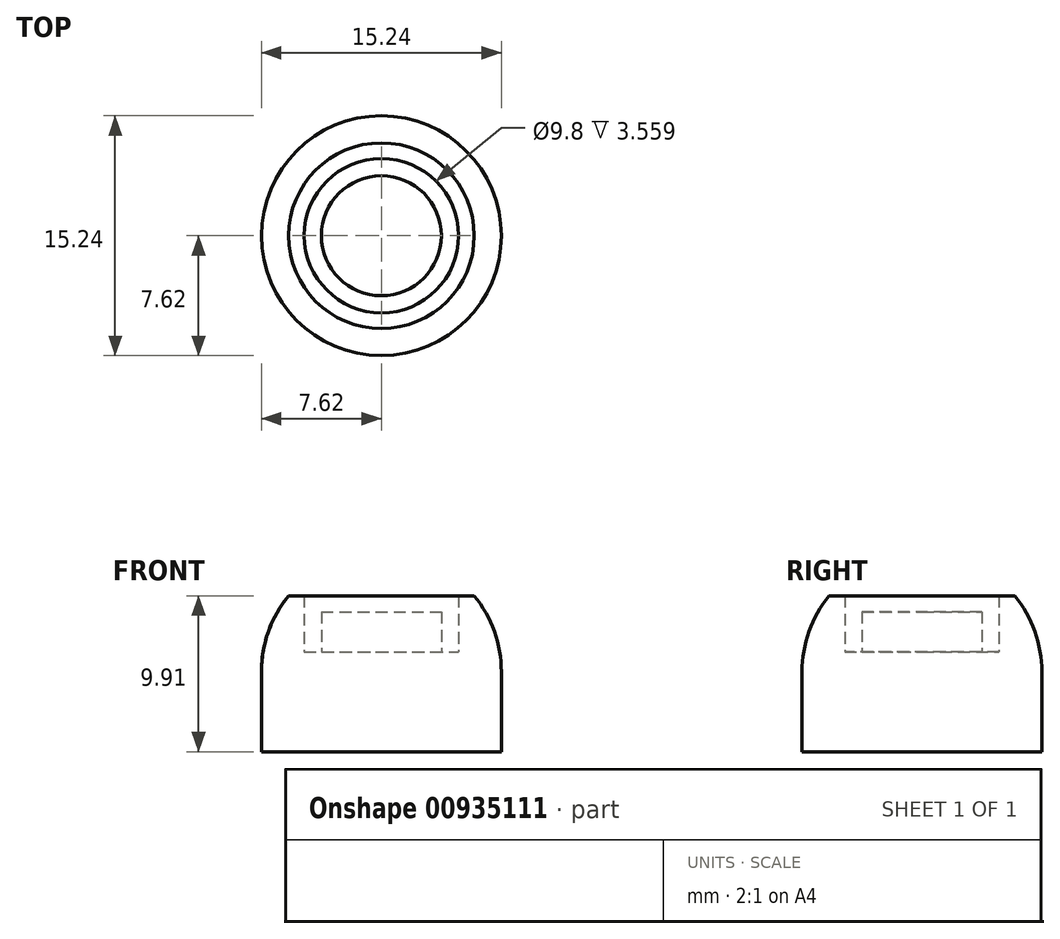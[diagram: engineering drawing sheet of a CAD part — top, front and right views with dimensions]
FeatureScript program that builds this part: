
annotation { "Feature Type Name" : "Feature", "Feature Type Description" : "" }
export const myFeature = defineFeature(function(context is Context, id is Id, definition is map)
    precondition{}
    {
        {
            var Q0;
            Q0=qCreatedBy(makeId("Front.planeOp"),FACE);
            var sketch = newSketch(context, id + "F0", { "sketchPlane" : qUnion([Q0])});
            skLineSegment(sketch, "E0", {"start": v(0, 0) * mm, "end": v(0, 2.54) * mm});
            skLineSegment(sketch, "E1", {"start": v(0, 2.54) * mm, "end": v(0, 6.35) * mm});
            skLineSegment(sketch, "E2", {"start": v(0, 6.35) * mm, "end": v(3.81, 6.35) * mm});
            skLineSegment(sketch, "E3", {"start": v(3.81, 6.35) * mm, "end": v(3.81, 3.81) * mm});
            skLineSegment(sketch, "E4", {"start": v(3.81, 3.81) * mm, "end": v(4.9, 3.81) * mm});
            skLineSegment(sketch, "E5", {"start": v(4.9, 3.81) * mm, "end": v(4.9, 7.37) * mm});
            skLineSegment(sketch, "E6", {"start": v(0, 0) * mm, "end": v(7.62, 0) * mm});
            skLineSegment(sketch, "E7", {"start": v(7.62, 0) * mm, "end": v(7.62, 2.54) * mm});
            skArc(sketch, "E8", {"start": v(7.62, 2.54) * mm, "mid": v(7.18, 5.1) * mm, "end": v(5.9, 7.37) * mm});
            skLineSegment(sketch, "E9", {"start": v(4.9, 7.37) * mm, "end": v(5.9, 7.37) * mm});
            skLineSegment(sketch, "E10", {"start": v(0, 0) * mm, "end": v(0, -2.54) * mm});
            skLineSegment(sketch, "E11", {"start": v(0, -2.54) * mm, "end": v(7.62, -2.54) * mm});
            skLineSegment(sketch, "E12", {"start": v(7.62, -2.54) * mm, "end": v(7.62, 0) * mm});
            skSolve(sketch);
        }
        {
            var Q0;
            Q0 = qSketchRegion(id + "F0", true);
            var Q1;
            Q1=sQuery(id+"F0.wireOp",EDGE,"E1");
            revolve(context, id + "F1", {"surfaceOperationType" : NewSurfaceOperationType.NEW, "entities" : qUnion([Q0]), "axis" : qUnion([Q1]), "revolveType" : RevolveType.FULL});
        }
        {
            var Q0;
            Q0=makeQuery(id+"F1.opRevolve","SWEPT_BODY",BODY,{"disambiguationData":[OSD([sQuery(id+"F0.wireOp",EDGE,"E0"),sQuery(id+"F0.wireOp",EDGE,"E1"),sQuery(id+"F0.wireOp",EDGE,"E2"),sQuery(id+"F0.wireOp",EDGE,"E3"),sQuery(id+"F0.wireOp",EDGE,"E4"),sQuery(id+"F0.wireOp",EDGE,"E5"),sQuery(id+"F0.wireOp",EDGE,"E7"),sQuery(id+"F0.wireOp",EDGE,"E8"),sQuery(id+"F0.wireOp",EDGE,"E9"),sQuery(id+"F0.wireOp",EDGE,"E10"),sQuery(id+"F0.wireOp",EDGE,"E11"),sQuery(id+"F0.wireOp",EDGE,"E12")])]});
            transform(context, id + "F2", {"entities" : qUnion([Q0]), "transformType" : TransformType.TRANSLATION_3D, "dx" : 25.4 * mm, "dy" : 0 * mm, "dz" : 0 * mm, "makeCopy" : true});
        }
        {
            var Q0;
            Q0=makeQuery(id+"F1.opRevolve","SWEPT_BODY",BODY,{"disambiguationData":[OSD([sQuery(id+"F0.wireOp",EDGE,"E0"),sQuery(id+"F0.wireOp",EDGE,"E1"),sQuery(id+"F0.wireOp",EDGE,"E2"),sQuery(id+"F0.wireOp",EDGE,"E3"),sQuery(id+"F0.wireOp",EDGE,"E4"),sQuery(id+"F0.wireOp",EDGE,"E5"),sQuery(id+"F0.wireOp",EDGE,"E7"),sQuery(id+"F0.wireOp",EDGE,"E8"),sQuery(id+"F0.wireOp",EDGE,"E9"),sQuery(id+"F0.wireOp",EDGE,"E10"),sQuery(id+"F0.wireOp",EDGE,"E11"),sQuery(id+"F0.wireOp",EDGE,"E12")])]});
            transform(context, id + "F3", {"entities" : qUnion([Q0]), "transformType" : TransformType.TRANSLATION_3D, "dx" : 0 * mm, "dy" : 25.4 * mm, "dz" : 0 * mm, "makeCopy" : true});
        }
        {
            var Q0;
            Q0=makeQuery(id+"F1.opRevolve","SWEPT_BODY",BODY,{"disambiguationData":[OSD([sQuery(id+"F0.wireOp",EDGE,"E0"),sQuery(id+"F0.wireOp",EDGE,"E1"),sQuery(id+"F0.wireOp",EDGE,"E2"),sQuery(id+"F0.wireOp",EDGE,"E3"),sQuery(id+"F0.wireOp",EDGE,"E4"),sQuery(id+"F0.wireOp",EDGE,"E5"),sQuery(id+"F0.wireOp",EDGE,"E7"),sQuery(id+"F0.wireOp",EDGE,"E8"),sQuery(id+"F0.wireOp",EDGE,"E9"),sQuery(id+"F0.wireOp",EDGE,"E10"),sQuery(id+"F0.wireOp",EDGE,"E11"),sQuery(id+"F0.wireOp",EDGE,"E12")])]});
            transform(context, id + "F4", {"entities" : qUnion([Q0]), "transformType" : TransformType.TRANSLATION_3D, "dx" : 0 * mm, "dy" : -25.4 * mm, "dz" : 0 * mm, "makeCopy" : true});
        }
        {
            var Q0;
            Q0=makeQuery(id+"F1.opRevolve","SWEPT_BODY",BODY,{"disambiguationData":[OSD([sQuery(id+"F0.wireOp",EDGE,"E0"),sQuery(id+"F0.wireOp",EDGE,"E1"),sQuery(id+"F0.wireOp",EDGE,"E2"),sQuery(id+"F0.wireOp",EDGE,"E3"),sQuery(id+"F0.wireOp",EDGE,"E4"),sQuery(id+"F0.wireOp",EDGE,"E5"),sQuery(id+"F0.wireOp",EDGE,"E7"),sQuery(id+"F0.wireOp",EDGE,"E8"),sQuery(id+"F0.wireOp",EDGE,"E9"),sQuery(id+"F0.wireOp",EDGE,"E10"),sQuery(id+"F0.wireOp",EDGE,"E11"),sQuery(id+"F0.wireOp",EDGE,"E12")])]});
            transform(context, id + "F5", {"entities" : qUnion([Q0]), "transformType" : TransformType.TRANSLATION_3D, "dx" : -25.4 * mm, "dy" : 0 * mm, "dz" : 0 * mm, "makeCopy" : true});
        }
        {
            var Q0;
            Q0=makeQuery(id+"F2.opPattern","COPY",BODY,{"derivedFrom":makeQuery(id+"F1.opRevolve","SWEPT_BODY",BODY,{"disambiguationData":[OSD([sQuery(id+"F0.wireOp",EDGE,"E0"),sQuery(id+"F0.wireOp",EDGE,"E1"),sQuery(id+"F0.wireOp",EDGE,"E2"),sQuery(id+"F0.wireOp",EDGE,"E3"),sQuery(id+"F0.wireOp",EDGE,"E4"),sQuery(id+"F0.wireOp",EDGE,"E5"),sQuery(id+"F0.wireOp",EDGE,"E7"),sQuery(id+"F0.wireOp",EDGE,"E8"),sQuery(id+"F0.wireOp",EDGE,"E9"),sQuery(id+"F0.wireOp",EDGE,"E10"),sQuery(id+"F0.wireOp",EDGE,"E11"),sQuery(id+"F0.wireOp",EDGE,"E12")])]}),"instanceName":"1"});
            transform(context, id + "F6", {"entities" : qUnion([Q0]), "transformType" : TransformType.TRANSLATION_3D, "dx" : 0 * mm, "dy" : 25.4 * mm, "dz" : 0 * mm, "makeCopy" : true});
        }
        {
            var Q0;
            Q0=makeQuery(id+"F2.opPattern","COPY",BODY,{"derivedFrom":makeQuery(id+"F1.opRevolve","SWEPT_BODY",BODY,{"disambiguationData":[OSD([sQuery(id+"F0.wireOp",EDGE,"E0"),sQuery(id+"F0.wireOp",EDGE,"E1"),sQuery(id+"F0.wireOp",EDGE,"E2"),sQuery(id+"F0.wireOp",EDGE,"E3"),sQuery(id+"F0.wireOp",EDGE,"E4"),sQuery(id+"F0.wireOp",EDGE,"E5"),sQuery(id+"F0.wireOp",EDGE,"E7"),sQuery(id+"F0.wireOp",EDGE,"E8"),sQuery(id+"F0.wireOp",EDGE,"E9"),sQuery(id+"F0.wireOp",EDGE,"E10"),sQuery(id+"F0.wireOp",EDGE,"E11"),sQuery(id+"F0.wireOp",EDGE,"E12")])]}),"instanceName":"1"});
            transform(context, id + "F7", {"entities" : qUnion([Q0]), "transformType" : TransformType.TRANSLATION_3D, "dx" : 0 * mm, "dy" : -25.4 * mm, "dz" : 0 * mm, "makeCopy" : true});
        }
        {
            var Q0;
            Q0=makeQuery(id+"F5.opPattern","COPY",BODY,{"derivedFrom":makeQuery(id+"F1.opRevolve","SWEPT_BODY",BODY,{"disambiguationData":[OSD([sQuery(id+"F0.wireOp",EDGE,"E0"),sQuery(id+"F0.wireOp",EDGE,"E1"),sQuery(id+"F0.wireOp",EDGE,"E2"),sQuery(id+"F0.wireOp",EDGE,"E3"),sQuery(id+"F0.wireOp",EDGE,"E4"),sQuery(id+"F0.wireOp",EDGE,"E5"),sQuery(id+"F0.wireOp",EDGE,"E7"),sQuery(id+"F0.wireOp",EDGE,"E8"),sQuery(id+"F0.wireOp",EDGE,"E9"),sQuery(id+"F0.wireOp",EDGE,"E10"),sQuery(id+"F0.wireOp",EDGE,"E11"),sQuery(id+"F0.wireOp",EDGE,"E12")])]}),"instanceName":"1"});
            transform(context, id + "F8", {"entities" : qUnion([Q0]), "transformType" : TransformType.TRANSLATION_3D, "dx" : 0 * mm, "dy" : -25.4 * mm, "dz" : 0 * mm, "makeCopy" : true});
        }
        {
            var Q0;
            Q0=makeQuery(id+"F5.opPattern","COPY",BODY,{"derivedFrom":makeQuery(id+"F1.opRevolve","SWEPT_BODY",BODY,{"disambiguationData":[OSD([sQuery(id+"F0.wireOp",EDGE,"E0"),sQuery(id+"F0.wireOp",EDGE,"E1"),sQuery(id+"F0.wireOp",EDGE,"E2"),sQuery(id+"F0.wireOp",EDGE,"E3"),sQuery(id+"F0.wireOp",EDGE,"E4"),sQuery(id+"F0.wireOp",EDGE,"E5"),sQuery(id+"F0.wireOp",EDGE,"E7"),sQuery(id+"F0.wireOp",EDGE,"E8"),sQuery(id+"F0.wireOp",EDGE,"E9"),sQuery(id+"F0.wireOp",EDGE,"E10"),sQuery(id+"F0.wireOp",EDGE,"E11"),sQuery(id+"F0.wireOp",EDGE,"E12")])]}),"instanceName":"1"});
            transform(context, id + "F9", {"entities" : qUnion([Q0]), "transformType" : TransformType.TRANSLATION_3D, "dx" : 0 * mm, "dy" : 25.4 * mm, "dz" : 0 * mm, "makeCopy" : true});
        }
        {
            var Q0;
            Q0=makeQuery(id+"F5.opPattern","COPY",BODY,{"derivedFrom":makeQuery(id+"F1.opRevolve","SWEPT_BODY",BODY,{"disambiguationData":[OSD([sQuery(id+"F0.wireOp",EDGE,"E0"),sQuery(id+"F0.wireOp",EDGE,"E1"),sQuery(id+"F0.wireOp",EDGE,"E2"),sQuery(id+"F0.wireOp",EDGE,"E3"),sQuery(id+"F0.wireOp",EDGE,"E4"),sQuery(id+"F0.wireOp",EDGE,"E5"),sQuery(id+"F0.wireOp",EDGE,"E7"),sQuery(id+"F0.wireOp",EDGE,"E8"),sQuery(id+"F0.wireOp",EDGE,"E9"),sQuery(id+"F0.wireOp",EDGE,"E10"),sQuery(id+"F0.wireOp",EDGE,"E11"),sQuery(id+"F0.wireOp",EDGE,"E12")])]}),"instanceName":"1"});
            transform(context, id + "F10", {"entities" : qUnion([Q0]), "transformType" : TransformType.TRANSLATION_3D, "dx" : -25.4 * mm, "dy" : 0 * mm, "dz" : 0 * mm, "makeCopy" : true});
        }
        {
            var Q0;
            Q0=makeQuery(id+"F2.opPattern","COPY",BODY,{"derivedFrom":makeQuery(id+"F1.opRevolve","SWEPT_BODY",BODY,{"disambiguationData":[OSD([sQuery(id+"F0.wireOp",EDGE,"E0"),sQuery(id+"F0.wireOp",EDGE,"E1"),sQuery(id+"F0.wireOp",EDGE,"E2"),sQuery(id+"F0.wireOp",EDGE,"E3"),sQuery(id+"F0.wireOp",EDGE,"E4"),sQuery(id+"F0.wireOp",EDGE,"E5"),sQuery(id+"F0.wireOp",EDGE,"E7"),sQuery(id+"F0.wireOp",EDGE,"E8"),sQuery(id+"F0.wireOp",EDGE,"E9"),sQuery(id+"F0.wireOp",EDGE,"E10"),sQuery(id+"F0.wireOp",EDGE,"E11"),sQuery(id+"F0.wireOp",EDGE,"E12")])]}),"instanceName":"1"});
            transform(context, id + "F11", {"entities" : qUnion([Q0]), "transformType" : TransformType.TRANSLATION_3D, "dx" : 25.4 * mm, "dy" : 0 * mm, "dz" : 0 * mm, "makeCopy" : true});
        }
        {
            var Q0;
            Q0=makeQuery(id+"F8.opPattern","COPY",BODY,{"derivedFrom":makeQuery(id+"F5.opPattern","COPY",BODY,{"derivedFrom":makeQuery(id+"F1.opRevolve","SWEPT_BODY",BODY,{"disambiguationData":[OSD([sQuery(id+"F0.wireOp",EDGE,"E0"),sQuery(id+"F0.wireOp",EDGE,"E1"),sQuery(id+"F0.wireOp",EDGE,"E2"),sQuery(id+"F0.wireOp",EDGE,"E3"),sQuery(id+"F0.wireOp",EDGE,"E4"),sQuery(id+"F0.wireOp",EDGE,"E5"),sQuery(id+"F0.wireOp",EDGE,"E7"),sQuery(id+"F0.wireOp",EDGE,"E8"),sQuery(id+"F0.wireOp",EDGE,"E9"),sQuery(id+"F0.wireOp",EDGE,"E10"),sQuery(id+"F0.wireOp",EDGE,"E11"),sQuery(id+"F0.wireOp",EDGE,"E12")])]}),"instanceName":"1"}),"instanceName":"1"});
            deleteBodies(context, id + "F12", {"entities" : qUnion([Q0])});
        }
        {
            var Q0;
            Q0=makeQuery(id+"F11.opPattern","COPY",BODY,{"derivedFrom":makeQuery(id+"F2.opPattern","COPY",BODY,{"derivedFrom":makeQuery(id+"F1.opRevolve","SWEPT_BODY",BODY,{"disambiguationData":[OSD([sQuery(id+"F0.wireOp",EDGE,"E0"),sQuery(id+"F0.wireOp",EDGE,"E1"),sQuery(id+"F0.wireOp",EDGE,"E2"),sQuery(id+"F0.wireOp",EDGE,"E3"),sQuery(id+"F0.wireOp",EDGE,"E4"),sQuery(id+"F0.wireOp",EDGE,"E5"),sQuery(id+"F0.wireOp",EDGE,"E7"),sQuery(id+"F0.wireOp",EDGE,"E8"),sQuery(id+"F0.wireOp",EDGE,"E9"),sQuery(id+"F0.wireOp",EDGE,"E10"),sQuery(id+"F0.wireOp",EDGE,"E11"),sQuery(id+"F0.wireOp",EDGE,"E12")])]}),"instanceName":"1"}),"instanceName":"1"});
            var Q1;
            Q1=makeQuery(id+"F10.opPattern","COPY",BODY,{"derivedFrom":makeQuery(id+"F5.opPattern","COPY",BODY,{"derivedFrom":makeQuery(id+"F1.opRevolve","SWEPT_BODY",BODY,{"disambiguationData":[OSD([sQuery(id+"F0.wireOp",EDGE,"E0"),sQuery(id+"F0.wireOp",EDGE,"E1"),sQuery(id+"F0.wireOp",EDGE,"E2"),sQuery(id+"F0.wireOp",EDGE,"E3"),sQuery(id+"F0.wireOp",EDGE,"E4"),sQuery(id+"F0.wireOp",EDGE,"E5"),sQuery(id+"F0.wireOp",EDGE,"E7"),sQuery(id+"F0.wireOp",EDGE,"E8"),sQuery(id+"F0.wireOp",EDGE,"E9"),sQuery(id+"F0.wireOp",EDGE,"E10"),sQuery(id+"F0.wireOp",EDGE,"E11"),sQuery(id+"F0.wireOp",EDGE,"E12")])]}),"instanceName":"1"}),"instanceName":"1"});
            var Q2;
            Q2=makeQuery(id+"F9.opPattern","COPY",BODY,{"derivedFrom":makeQuery(id+"F5.opPattern","COPY",BODY,{"derivedFrom":makeQuery(id+"F1.opRevolve","SWEPT_BODY",BODY,{"disambiguationData":[OSD([sQuery(id+"F0.wireOp",EDGE,"E0"),sQuery(id+"F0.wireOp",EDGE,"E1"),sQuery(id+"F0.wireOp",EDGE,"E2"),sQuery(id+"F0.wireOp",EDGE,"E3"),sQuery(id+"F0.wireOp",EDGE,"E4"),sQuery(id+"F0.wireOp",EDGE,"E5"),sQuery(id+"F0.wireOp",EDGE,"E7"),sQuery(id+"F0.wireOp",EDGE,"E8"),sQuery(id+"F0.wireOp",EDGE,"E9"),sQuery(id+"F0.wireOp",EDGE,"E10"),sQuery(id+"F0.wireOp",EDGE,"E11"),sQuery(id+"F0.wireOp",EDGE,"E12")])]}),"instanceName":"1"}),"instanceName":"1"});
            var Q3;
            Q3=makeQuery(id+"F7.opPattern","COPY",BODY,{"derivedFrom":makeQuery(id+"F2.opPattern","COPY",BODY,{"derivedFrom":makeQuery(id+"F1.opRevolve","SWEPT_BODY",BODY,{"disambiguationData":[OSD([sQuery(id+"F0.wireOp",EDGE,"E0"),sQuery(id+"F0.wireOp",EDGE,"E1"),sQuery(id+"F0.wireOp",EDGE,"E2"),sQuery(id+"F0.wireOp",EDGE,"E3"),sQuery(id+"F0.wireOp",EDGE,"E4"),sQuery(id+"F0.wireOp",EDGE,"E5"),sQuery(id+"F0.wireOp",EDGE,"E7"),sQuery(id+"F0.wireOp",EDGE,"E8"),sQuery(id+"F0.wireOp",EDGE,"E9"),sQuery(id+"F0.wireOp",EDGE,"E10"),sQuery(id+"F0.wireOp",EDGE,"E11"),sQuery(id+"F0.wireOp",EDGE,"E12")])]}),"instanceName":"1"}),"instanceName":"1"});
            deleteBodies(context, id + "F13", {"entities" : qUnion([Q0, Q1, Q2, Q3])});
        }
        {
            var Q0;
            Q0=makeQuery(id+"F6.opPattern","COPY",BODY,{"derivedFrom":makeQuery(id+"F2.opPattern","COPY",BODY,{"derivedFrom":makeQuery(id+"F1.opRevolve","SWEPT_BODY",BODY,{"disambiguationData":[OSD([sQuery(id+"F0.wireOp",EDGE,"E0"),sQuery(id+"F0.wireOp",EDGE,"E1"),sQuery(id+"F0.wireOp",EDGE,"E2"),sQuery(id+"F0.wireOp",EDGE,"E3"),sQuery(id+"F0.wireOp",EDGE,"E4"),sQuery(id+"F0.wireOp",EDGE,"E5"),sQuery(id+"F0.wireOp",EDGE,"E7"),sQuery(id+"F0.wireOp",EDGE,"E8"),sQuery(id+"F0.wireOp",EDGE,"E9"),sQuery(id+"F0.wireOp",EDGE,"E10"),sQuery(id+"F0.wireOp",EDGE,"E11"),sQuery(id+"F0.wireOp",EDGE,"E12")])]}),"instanceName":"1"}),"instanceName":"1"});
            var Q1;
            Q1=makeQuery(id+"F5.opPattern","COPY",BODY,{"derivedFrom":makeQuery(id+"F1.opRevolve","SWEPT_BODY",BODY,{"disambiguationData":[OSD([sQuery(id+"F0.wireOp",EDGE,"E0"),sQuery(id+"F0.wireOp",EDGE,"E1"),sQuery(id+"F0.wireOp",EDGE,"E2"),sQuery(id+"F0.wireOp",EDGE,"E3"),sQuery(id+"F0.wireOp",EDGE,"E4"),sQuery(id+"F0.wireOp",EDGE,"E5"),sQuery(id+"F0.wireOp",EDGE,"E7"),sQuery(id+"F0.wireOp",EDGE,"E8"),sQuery(id+"F0.wireOp",EDGE,"E9"),sQuery(id+"F0.wireOp",EDGE,"E10"),sQuery(id+"F0.wireOp",EDGE,"E11"),sQuery(id+"F0.wireOp",EDGE,"E12")])]}),"instanceName":"1"});
            var Q2;
            Q2=makeQuery(id+"F4.opPattern","COPY",BODY,{"derivedFrom":makeQuery(id+"F1.opRevolve","SWEPT_BODY",BODY,{"disambiguationData":[OSD([sQuery(id+"F0.wireOp",EDGE,"E0"),sQuery(id+"F0.wireOp",EDGE,"E1"),sQuery(id+"F0.wireOp",EDGE,"E2"),sQuery(id+"F0.wireOp",EDGE,"E3"),sQuery(id+"F0.wireOp",EDGE,"E4"),sQuery(id+"F0.wireOp",EDGE,"E5"),sQuery(id+"F0.wireOp",EDGE,"E7"),sQuery(id+"F0.wireOp",EDGE,"E8"),sQuery(id+"F0.wireOp",EDGE,"E9"),sQuery(id+"F0.wireOp",EDGE,"E10"),sQuery(id+"F0.wireOp",EDGE,"E11"),sQuery(id+"F0.wireOp",EDGE,"E12")])]}),"instanceName":"1"});
            var Q3;
            Q3=makeQuery(id+"F3.opPattern","COPY",BODY,{"derivedFrom":makeQuery(id+"F1.opRevolve","SWEPT_BODY",BODY,{"disambiguationData":[OSD([sQuery(id+"F0.wireOp",EDGE,"E0"),sQuery(id+"F0.wireOp",EDGE,"E1"),sQuery(id+"F0.wireOp",EDGE,"E2"),sQuery(id+"F0.wireOp",EDGE,"E3"),sQuery(id+"F0.wireOp",EDGE,"E4"),sQuery(id+"F0.wireOp",EDGE,"E5"),sQuery(id+"F0.wireOp",EDGE,"E7"),sQuery(id+"F0.wireOp",EDGE,"E8"),sQuery(id+"F0.wireOp",EDGE,"E9"),sQuery(id+"F0.wireOp",EDGE,"E10"),sQuery(id+"F0.wireOp",EDGE,"E11"),sQuery(id+"F0.wireOp",EDGE,"E12")])]}),"instanceName":"1"});
            deleteBodies(context, id + "F14", {"entities" : qUnion([Q0, Q1, Q2, Q3])});
        }
        {
            var Q0;
            Q0=makeQuery(id+"F2.opPattern","COPY",BODY,{"derivedFrom":makeQuery(id+"F1.opRevolve","SWEPT_BODY",BODY,{"disambiguationData":[OSD([sQuery(id+"F0.wireOp",EDGE,"E0"),sQuery(id+"F0.wireOp",EDGE,"E1"),sQuery(id+"F0.wireOp",EDGE,"E2"),sQuery(id+"F0.wireOp",EDGE,"E3"),sQuery(id+"F0.wireOp",EDGE,"E4"),sQuery(id+"F0.wireOp",EDGE,"E5"),sQuery(id+"F0.wireOp",EDGE,"E7"),sQuery(id+"F0.wireOp",EDGE,"E8"),sQuery(id+"F0.wireOp",EDGE,"E9"),sQuery(id+"F0.wireOp",EDGE,"E10"),sQuery(id+"F0.wireOp",EDGE,"E11"),sQuery(id+"F0.wireOp",EDGE,"E12")])]}),"instanceName":"1"});
            deleteBodies(context, id + "F15", {"entities" : qUnion([Q0])});
        }
    });
